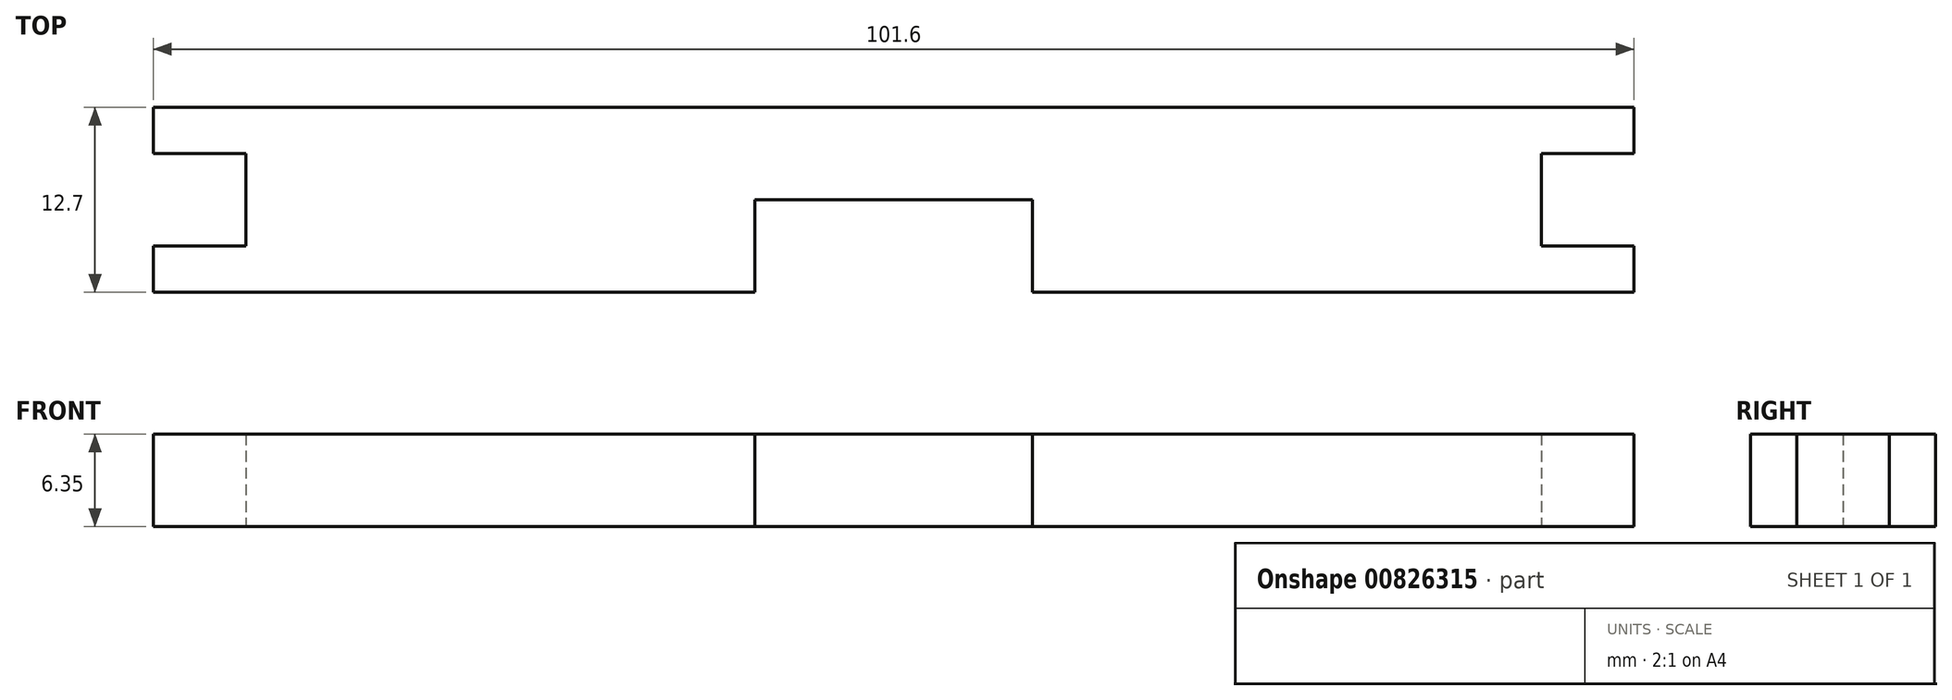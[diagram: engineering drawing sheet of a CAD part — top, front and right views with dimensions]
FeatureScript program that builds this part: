
annotation { "Feature Type Name" : "Feature", "Feature Type Description" : "" }
export const myFeature = defineFeature(function(context is Context, id is Id, definition is map)
    precondition{}
    {
        {
            var Q0;
            Q0=qCreatedBy(makeId("Top.planeOp"),FACE);
            var sketch = newSketch(context, id + "F0", { "sketchPlane" : qUnion([Q0])});
            skLineSegment(sketch, "E0.bottom", {"start": v(0, 0) * mm, "end": v(101.6, 0) * mm});
            skLineSegment(sketch, "E0.top", {"start": v(0, -12.7) * mm, "end": v(41.28, -12.7) * mm});
            skLineSegment(sketch, "E0.left", {"start": v(0, 0) * mm, "end": v(0, -3.17) * mm});
            skLineSegment(sketch, "E0.right", {"start": v(101.6, 0) * mm, "end": v(101.6, -3.17) * mm});
            skLineSegment(sketch, "E1", {"start": v(41.28, -12.7) * mm, "end": v(41.28, -6.35) * mm});
            skLineSegment(sketch, "E2", {"start": v(41.28, -6.35) * mm, "end": v(60.33, -6.35) * mm});
            skLineSegment(sketch, "E3", {"start": v(60.33, -6.35) * mm, "end": v(60.33, -12.7) * mm});
            skLineSegment(sketch, "E4", {"start": v(60.33, -12.7) * mm, "end": v(101.6, -12.7) * mm});
            skLineSegment(sketch, "E5", {"start": v(0, -3.17) * mm, "end": v(6.35, -3.17) * mm});
            skLineSegment(sketch, "E6", {"start": v(6.35, -3.17) * mm, "end": v(6.35, -9.53) * mm});
            skLineSegment(sketch, "E7", {"start": v(6.35, -9.53) * mm, "end": v(0, -9.53) * mm});
            skLineSegment(sketch, "E8.trimOffspring", {"start": v(0, -9.53) * mm, "end": v(0, -12.7) * mm});
            skLineSegment(sketch, "E9", {"start": v(50.8, 0) * mm, "end": v(50.8, -2.54) * mm, "construction": true});
            skLineSegment(sketch, "E10.MirrorCS", {"start": v(101.6, -3.17) * mm, "end": v(95.25, -3.17) * mm});
            skLineSegment(sketch, "E11.MirrorCS", {"start": v(95.25, -3.17) * mm, "end": v(95.25, -9.53) * mm});
            skLineSegment(sketch, "E12.MirrorCS", {"start": v(95.25, -9.53) * mm, "end": v(101.6, -9.53) * mm});
            skLineSegment(sketch, "E13.MirrorCS", {"start": v(101.6, -9.53) * mm, "end": v(101.6, -12.7) * mm});
            skSolve(sketch);
        }
        {
            var Q0;
            Q0=makeQuery(id+"F0.imprint","IMPRINT",FACE,{"disambiguationData":[TD([[makeQuery(id+"F0.imprint","IMPRINT",EDGE,{"derivedFrom":sQuery(id+"F0.wireOp",EDGE,"E0.bottom")}),-1.0]])]});
            extrude(context, id + "F1", {"entities" : qUnion([Q0]), "depth" : 6.35 * mm, "offsetDistance" : 25.4 * mm});
        }
    });
